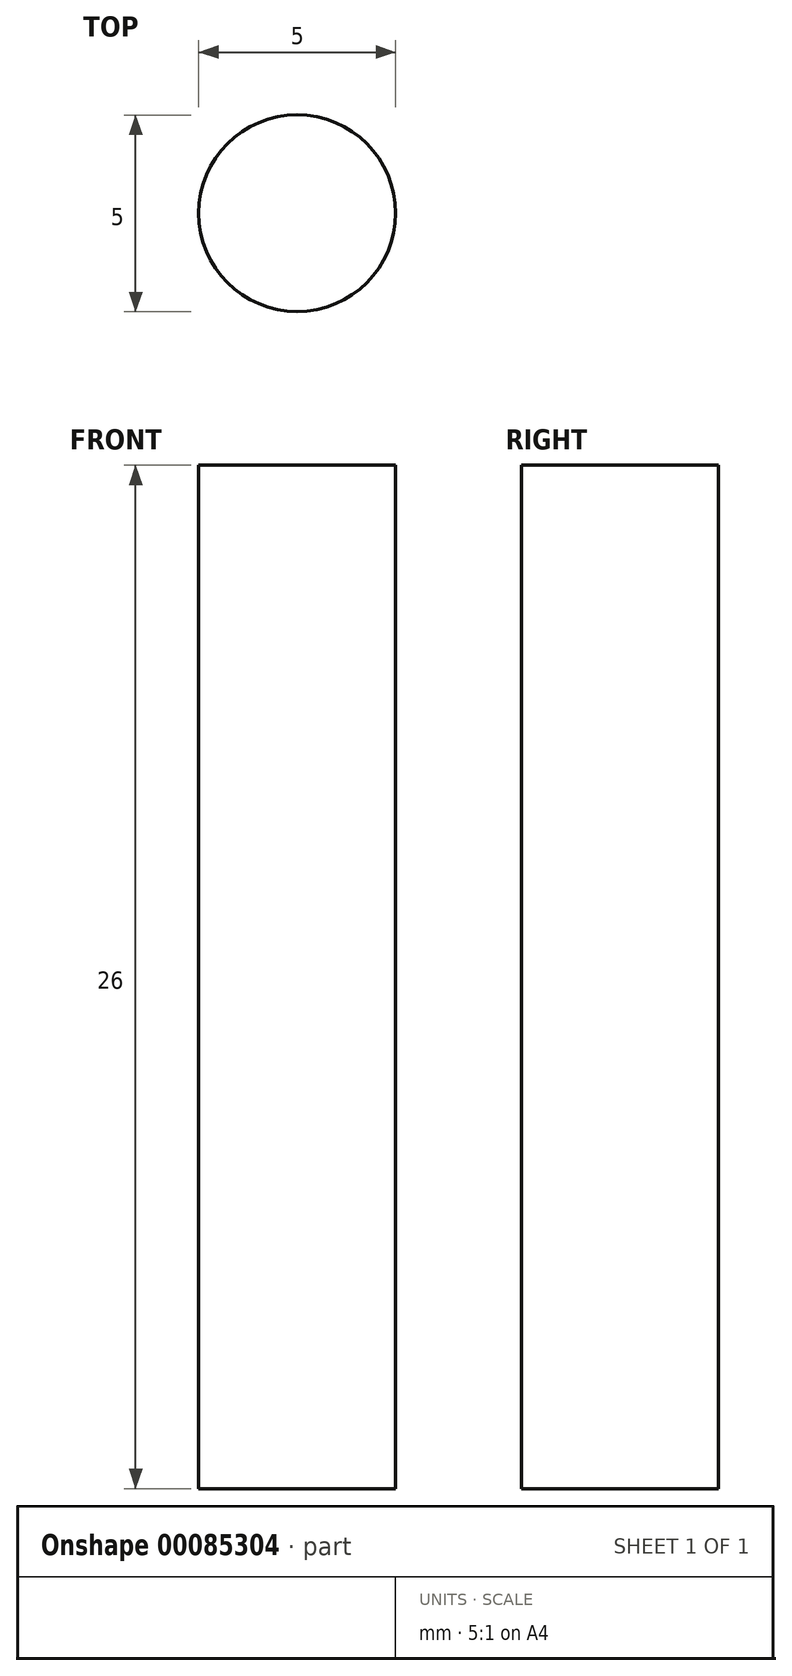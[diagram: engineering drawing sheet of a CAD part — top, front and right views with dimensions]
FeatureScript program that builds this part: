
annotation { "Feature Type Name" : "Feature", "Feature Type Description" : "" }
export const myFeature = defineFeature(function(context is Context, id is Id, definition is map)
    precondition{}
    {
        {
            var Q0;
            Q0=qCreatedBy(makeId("Top.planeOp"),FACE);
            var sketch = newSketch(context, id + "F0", { "sketchPlane" : qUnion([Q0])});
            skCircle(sketch, "E0", {"center": v(0, -0.22) * mm, "radius": 2.5 * mm});
            skSolve(sketch);
        }
        {
            var Q0;
            Q0=qSketchRegion(id+"F0",true);
            extrude(context, id + "F1", {"entities" : qUnion([Q0]), "depth" : 26 * mm});
        }
    });
